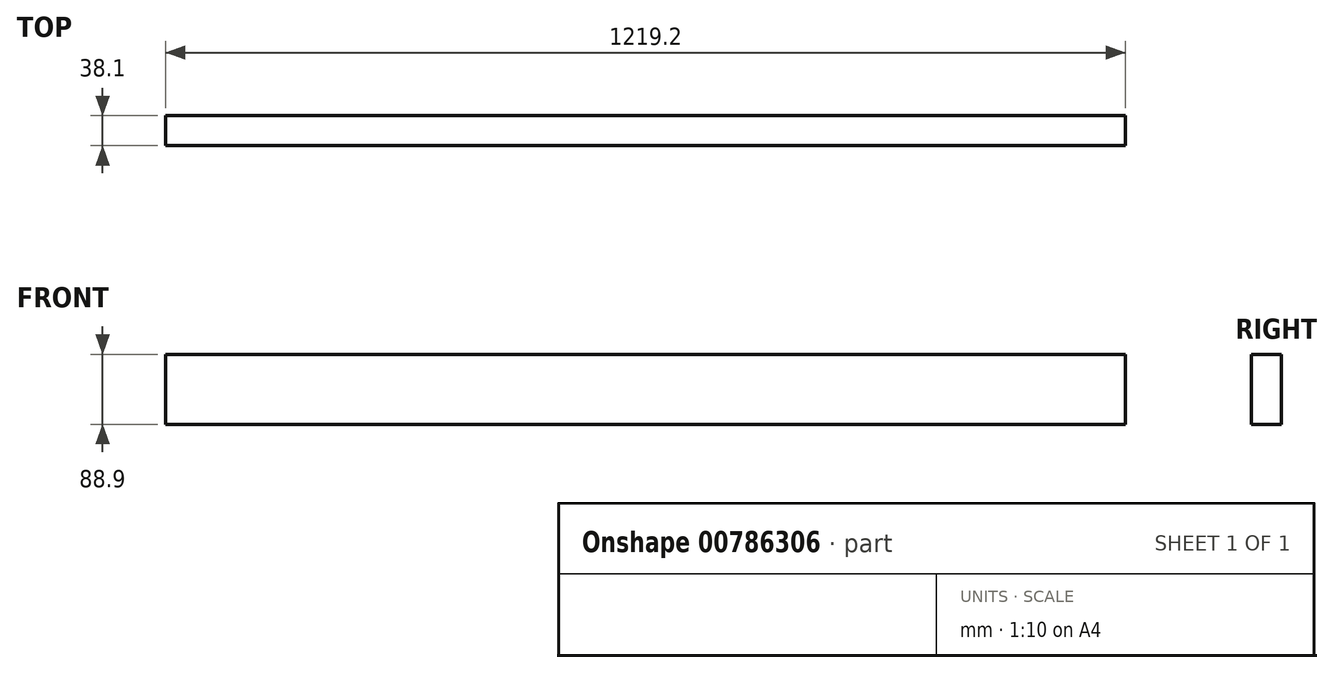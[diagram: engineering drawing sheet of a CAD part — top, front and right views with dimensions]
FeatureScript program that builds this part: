
annotation { "Feature Type Name" : "Feature", "Feature Type Description" : "" }
export const myFeature = defineFeature(function(context is Context, id is Id, definition is map)
    precondition{}
    {
        {
            var Q0;
            Q0=qCreatedBy(makeId("Front.planeOp"),FACE);
            var sketch = newSketch(context, id + "F0", { "sketchPlane" : qUnion([Q0])});
            skLineSegment(sketch, "E0.bottom", {"start": v(-609.6, 44.45) * mm, "end": v(609.6, 44.45) * mm});
            skLineSegment(sketch, "E0.top", {"start": v(-609.6, -44.45) * mm, "end": v(609.6, -44.45) * mm});
            skLineSegment(sketch, "E0.left", {"start": v(-609.6, 44.45) * mm, "end": v(-609.6, -44.45) * mm});
            skLineSegment(sketch, "E0.right", {"start": v(609.6, 44.45) * mm, "end": v(609.6, -44.45) * mm});
            skPoint(sketch, "E0.middle", {"position": v(0, 0) * mm});
            skSolve(sketch);
        }
        {
            var Q0;
            Q0=makeQuery(id+"F0.imprint","IMPRINT",FACE,{"disambiguationData":[TD([[makeQuery(id+"F0.imprint","IMPRINT",EDGE,{"derivedFrom":sQuery(id+"F0.wireOp",EDGE,"E0.bottom")}),-1.0]])]});
            extrude(context, id + "F1", {"entities" : qUnion([Q0]), "endBound" : BoundingType.SYMMETRIC, "depth" : 38.1 * mm, "offsetDistance" : 25.4 * mm});
        }
    });
